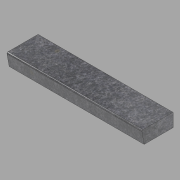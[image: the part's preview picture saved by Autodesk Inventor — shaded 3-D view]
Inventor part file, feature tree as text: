
AUTODESK INVENTOR PART (.ipt)
format: ipt  version: 2022.1 (Build 261234020, 234B)  size: 98,816 bytes
history: native  units: in
note: dims shown in document units (in); Inventor stores cm internally (conversion verified against a paired STEP export)
features: other x3, extrude x1, sketch x1
ambient origin geometry x8: Origin, YZ Plane, XZ Plane, XY Plane, X Axis, Y Axis, Z Axis, Center Point
bodies: Solid1 (feature_tree)
feature tree (5):
  other  "Blocks"
  extrude  "Extrusion1"  Depth=60.75in TaperAngle=0.0deg
  sketch  "Sketch1"  dims[d0=13.0in d1=6.0in d2=13.5in d3=0.5in d4=0.5in d5=60.75in d6=0.0in]
  other  "Profile"
  other  "Profile:1"
